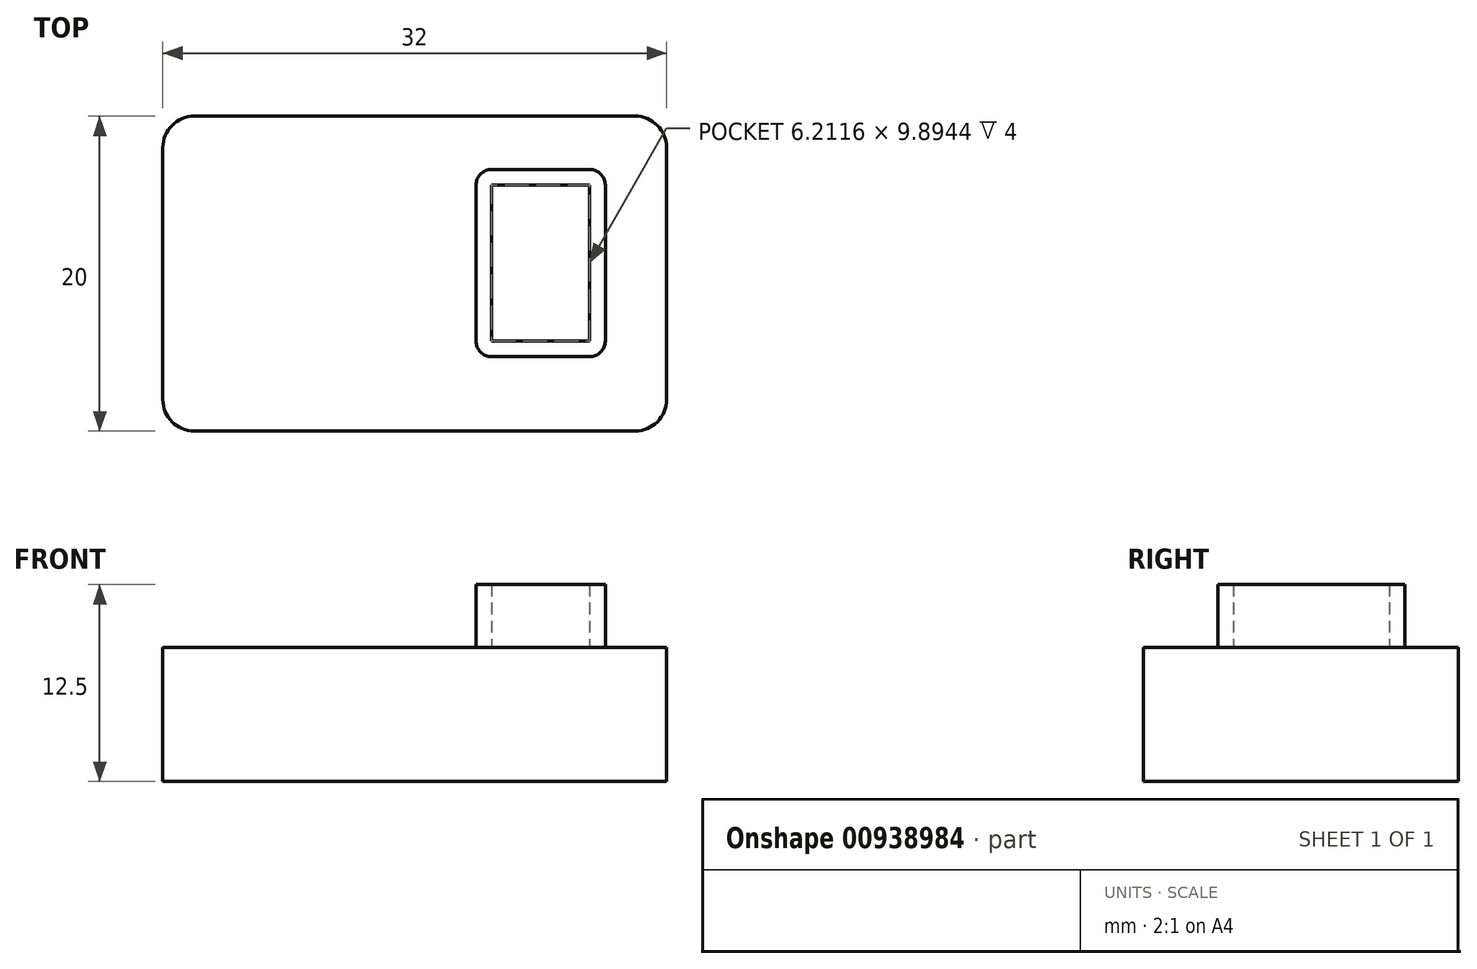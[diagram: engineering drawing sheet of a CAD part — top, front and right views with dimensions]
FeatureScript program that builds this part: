
annotation { "Feature Type Name" : "Feature", "Feature Type Description" : "" }
export const myFeature = defineFeature(function(context is Context, id is Id, definition is map)
    precondition{}
    {
        {
            var Q0;
            Q0=qCreatedBy(makeId("Top.planeOp"),FACE);
            var sketch = newSketch(context, id + "F0", { "sketchPlane" : qUnion([Q0])});
            skLineSegment(sketch, "E0.bottom", {"start": v(14, 9.33) * mm, "end": v(-14, 9.33) * mm});
            skLineSegment(sketch, "E0.top", {"start": v(14, -10.67) * mm, "end": v(-14, -10.67) * mm});
            skLineSegment(sketch, "E0.left", {"start": v(16, 7.33) * mm, "end": v(16, -8.67) * mm});
            skLineSegment(sketch, "E0.right", {"start": v(-16, 7.33) * mm, "end": v(-16, -8.67) * mm});
            skPoint(sketch, "E0.middle", {"position": v(0, -0.67) * mm});
            skPoint(sketch, "E1.visualSharp", {"position": v(-16, 9.33) * mm});
            skArc(sketch, "E1.filletArc", {"start": v(-14, 9.33) * mm, "mid": v(-15.41, 8.74) * mm, "end": v(-16, 7.33) * mm});
            skPoint(sketch, "E2.visualSharp", {"position": v(16, 9.33) * mm});
            skArc(sketch, "E2.filletArc", {"start": v(16, 7.33) * mm, "mid": v(15.41, 8.74) * mm, "end": v(14, 9.33) * mm});
            skPoint(sketch, "E3.visualSharp", {"position": v(16, -10.67) * mm});
            skArc(sketch, "E3.filletArc", {"start": v(14, -10.67) * mm, "mid": v(15.41, -10.08) * mm, "end": v(16, -8.67) * mm});
            skPoint(sketch, "E4.visualSharp", {"position": v(-16, -10.67) * mm});
            skArc(sketch, "E4.filletArc", {"start": v(-16, -8.67) * mm, "mid": v(-15.41, -10.08) * mm, "end": v(-14, -10.67) * mm});
            skSolve(sketch);
        }
        {
            var Q0;
            Q0=makeQuery(id+"F0.imprint","IMPRINT",FACE,{"disambiguationData":[TD([[makeQuery(id+"F0.imprint","IMPRINT",EDGE,{"derivedFrom":sQuery(id+"F0.wireOp",EDGE,"E0.bottom")}),1.0]])]});
            extrude(context, id + "F1", {"entities" : qUnion([Q0]), "depth" : 8.5 * mm, "offsetDistance" : 25 * mm});
        }
        {
            var Q0;
            Q0=makeQuery(id+"F1.opExtrude","CAP_FACE",FACE,{"disambiguationData":[OSD([sQuery(id+"F0.wireOp",EDGE,"E0.bottom"),sQuery(id+"F0.wireOp",EDGE,"E0.top"),sQuery(id+"F0.wireOp",EDGE,"E0.left"),sQuery(id+"F0.wireOp",EDGE,"E0.right"),sQuery(id+"F0.wireOp",EDGE,"E1.filletArc"),sQuery(id+"F0.wireOp",EDGE,"E2.filletArc"),sQuery(id+"F0.wireOp",EDGE,"E3.filletArc"),sQuery(id+"F0.wireOp",EDGE,"E4.filletArc")])],"isStart":false});
            var sketch = newSketch(context, id + "F2", { "sketchPlane" : qUnion([Q0])});
            skLineSegment(sketch, "E5.bottom", {"start": v(11.1, 5.95) * mm, "end": v(4.9, 5.95) * mm});
            skLineSegment(sketch, "E5.top", {"start": v(11.1, -5.95) * mm, "end": v(4.9, -5.95) * mm});
            skLineSegment(sketch, "E5.left", {"start": v(12.1, 4.95) * mm, "end": v(12.1, -4.95) * mm});
            skLineSegment(sketch, "E5.right", {"start": v(3.9, 4.95) * mm, "end": v(3.9, -4.95) * mm});
            skPoint(sketch, "E5.middle", {"position": v(8, 0) * mm});
            skLineSegment(sketch, "E6.0", {"start": v(11.1, 4.95) * mm, "end": v(4.9, 4.95) * mm});
            skLineSegment(sketch, "E6.1", {"start": v(11.1, 4.95) * mm, "end": v(11.1, -4.95) * mm});
            skLineSegment(sketch, "E6.2", {"start": v(11.1, -4.95) * mm, "end": v(4.9, -4.95) * mm});
            skLineSegment(sketch, "E6.3", {"start": v(4.9, 4.95) * mm, "end": v(4.9, -4.95) * mm});
            skPoint(sketch, "E7.visualSharp", {"position": v(3.9, 5.95) * mm});
            skArc(sketch, "E7.filletArc", {"start": v(4.9, 5.95) * mm, "mid": v(4.19, 5.65) * mm, "end": v(3.9, 4.95) * mm});
            skPoint(sketch, "E8.visualSharp", {"position": v(12.1, 5.95) * mm});
            skArc(sketch, "E8.filletArc", {"start": v(12.1, 4.95) * mm, "mid": v(11.81, 5.65) * mm, "end": v(11.1, 5.95) * mm});
            skPoint(sketch, "E9.visualSharp", {"position": v(12.1, -5.95) * mm});
            skArc(sketch, "E9.filletArc", {"start": v(11.1, -5.95) * mm, "mid": v(11.81, -5.65) * mm, "end": v(12.1, -4.95) * mm});
            skPoint(sketch, "E10.visualSharp", {"position": v(3.9, -5.95) * mm});
            skArc(sketch, "E10.filletArc", {"start": v(3.9, -4.95) * mm, "mid": v(4.19, -5.65) * mm, "end": v(4.9, -5.95) * mm});
            skSolve(sketch);
        }
        {
            var Q0;
            Q0=makeQuery(id+"F2.imprint","IMPRINT",FACE,{"disambiguationData":[TD([[makeQuery(id+"F2.imprint","IMPRINT",EDGE,{"derivedFrom":sQuery(id+"F2.wireOp",EDGE,"E5.bottom")}),1.0]])]});
            extrude(context, id + "F3", {"entities" : qUnion([Q0]), "operationType" : NewBodyOperationType.ADD, "depth" : 4 * mm, "offsetDistance" : 25 * mm});
        }
    });
